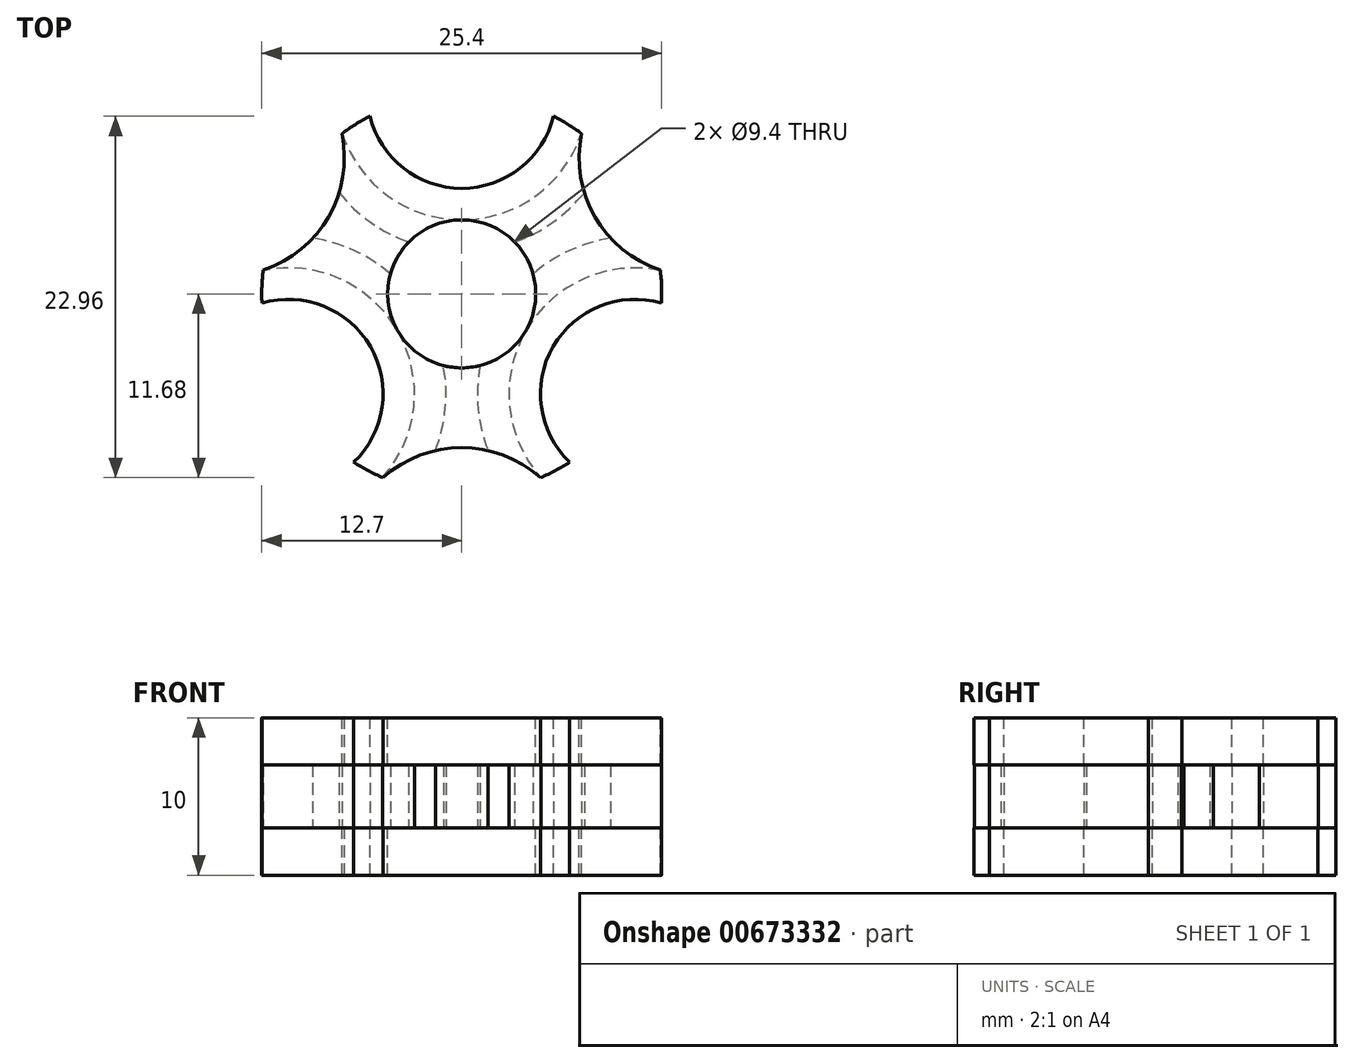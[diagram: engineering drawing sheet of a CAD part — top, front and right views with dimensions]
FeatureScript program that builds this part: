
annotation { "Feature Type Name" : "Feature", "Feature Type Description" : "" }
export const myFeature = defineFeature(function(context is Context, id is Id, definition is map)
    precondition{}
    {
        {
            var Q0;
            Q0=qCreatedBy(makeId("Top.planeOp"),FACE);
            var sketch = newSketch(context, id + "F0", { "sketchPlane" : qUnion([Q0])});
            skLineSegment(sketch, "E0", {"start": v(0, 56.08) * mm, "end": v(0, 0) * mm, "construction": true});
            skLineSegment(sketch, "E1", {"start": v(0, 0) * mm, "end": v(54.15, -31.26) * mm, "construction": true});
            skLineSegment(sketch, "E2", {"start": v(-60, -34.64) * mm, "end": v(0, 0) * mm, "construction": true});
            skLineSegment(sketch, "E3", {"start": v(-56.98, 32.9) * mm, "end": v(-8.46, 4.89) * mm, "construction": true});
            skLineSegment(sketch, "E4", {"start": v(48.6, 28.06) * mm, "end": v(8.46, 4.89) * mm, "construction": true});
            skLineSegment(sketch, "E5", {"start": v(0, -60) * mm, "end": v(0, -9.77) * mm, "construction": true});
            skArc(sketch, "E6", {"start": v(-6.86, -10.7) * mm, "mid": v(-5.8, -3.35) * mm, "end": v(-12.69, -0.6) * mm});
            skArc(sketch, "E7", {"start": v(12.69, -0.6) * mm, "mid": v(5.8, -3.35) * mm, "end": v(6.86, -10.7) * mm});
            skArc(sketch, "E8", {"start": v(-5.83, 11.28) * mm, "mid": v(0, 6.7) * mm, "end": v(5.83, 11.28) * mm});
            skArc(sketch, "E9", {"start": v(-7.6, 10.18) * mm, "mid": v(0, 4.7) * mm, "end": v(7.6, 10.18) * mm});
            skArc(sketch, "E10", {"start": v(12.61, 1.48) * mm, "mid": v(4.07, -2.35) * mm, "end": v(5.02, -11.67) * mm});
            skArc(sketch, "E11", {"start": v(-5.32, -11.99) * mm, "mid": v(-3.96, -2.54) * mm, "end": v(-12.61, 1.48) * mm});
            skArc(sketch, "E12", {"start": v(-5.83, 11.28) * mm, "mid": v(-6.75, 10.76) * mm, "end": v(-7.61, 10.17) * mm});
            skCircle(sketch, "E13", {"center": v(0, 0) * mm, "radius": 4.7 * mm});
            skArc(sketch, "E14", {"start": v(-12.61, 1.51) * mm, "mid": v(-8.46, 4.89) * mm, "end": v(-7.61, 10.17) * mm});
            skArc(sketch, "E15", {"start": v(1.16, -4.56) * mm, "mid": v(1.04, -7.3) * mm, "end": v(1.67, -9.96) * mm});
            skArc(sketch, "E16", {"start": v(-7.79, 6.43) * mm, "mid": v(-5.8, 4.55) * mm, "end": v(-3.36, 3.28) * mm});
            skArc(sketch, "E17.trimOffspring", {"start": v(7.61, 10.17) * mm, "mid": v(8.46, 4.89) * mm, "end": v(12.61, 1.51) * mm});
            skArc(sketch, "E18.trimOffspring", {"start": v(-12.61, 1.51) * mm, "mid": v(-12.7, 0.46) * mm, "end": v(-12.69, -0.6) * mm});
            skArc(sketch, "E19.trimOffspring", {"start": v(-6.86, -10.7) * mm, "mid": v(-5.95, -11.22) * mm, "end": v(-5, -11.68) * mm});
            skArc(sketch, "E20.trimOffspring", {"start": v(-4.53, 1.27) * mm, "mid": v(-6.84, 2.74) * mm, "end": v(-9.46, 3.53) * mm});
            skArc(sketch, "E21.trimOffspring", {"start": v(3.36, 3.28) * mm, "mid": v(5.8, 4.55) * mm, "end": v(7.79, 6.43) * mm});
            skArc(sketch, "E22.trimOffspring", {"start": v(12.69, -0.6) * mm, "mid": v(12.7, 0.46) * mm, "end": v(12.61, 1.51) * mm});
            skArc(sketch, "E23.trimOffspring", {"start": v(5, -11.68) * mm, "mid": v(5.95, -11.22) * mm, "end": v(6.86, -10.7) * mm});
            skArc(sketch, "E24.trimOffspring", {"start": v(7.61, 10.17) * mm, "mid": v(6.75, 10.76) * mm, "end": v(5.83, 11.28) * mm});
            skArc(sketch, "E25.trimOffspring", {"start": v(-1.67, -9.96) * mm, "mid": v(-1.04, -7.3) * mm, "end": v(-1.16, -4.56) * mm});
            skArc(sketch, "E26.trimOffspring", {"start": v(5, -11.68) * mm, "mid": v(-0.22, -9.77) * mm, "end": v(-5.32, -11.99) * mm});
            skArc(sketch, "E27.trimOffspring", {"start": v(9.46, 3.53) * mm, "mid": v(6.84, 2.74) * mm, "end": v(4.53, 1.27) * mm});
            skLineSegment(sketch, "E28.trimOffspring", {"start": v(-4.07, 2.35) * mm, "end": v(0, 0) * mm, "construction": true});
            skLineSegment(sketch, "E29.trimOffspring", {"start": v(4.07, 2.35) * mm, "end": v(0, 0) * mm, "construction": true});
            skLineSegment(sketch, "E30.trimOffspring", {"start": v(0, -4.7) * mm, "end": v(0, 0) * mm, "construction": true});
            skSolve(sketch);
        }
        {
            var Q0;
            {var subQ5=sQuery(id+"F0.wireOp",EDGE,"E6");Q0=makeQuery(id+"F0.imprint","IMPRINT",FACE,{"disambiguationData":[TD([[makeQuery(id+"F0.imprint","IMPRINT",EDGE,{"derivedFrom":subQ5}),-1.0]])]});}
            var Q1;
            {var subQ3=sQuery(id+"F0.wireOp",EDGE,"E20.trimOffspring");Q1=makeQuery(id+"F0.imprint","IMPRINT",FACE,{"disambiguationData":[TD([[makeQuery(id+"F0.imprint","IMPRINT",EDGE,{"derivedFrom":subQ3}),1.0]])]});}
            var Q2;
            {var subQ0=sQuery(id+"F0.wireOp",EDGE,"E16");Q2=makeQuery(id+"F0.imprint","IMPRINT",FACE,{"disambiguationData":[TD([[makeQuery(id+"F0.imprint","IMPRINT",EDGE,{"derivedFrom":subQ0}),-1.0]])]});}
            var Q3;
            {var subQ0=sQuery(id+"F0.wireOp",EDGE,"E16");Q3=makeQuery(id+"F0.imprint","IMPRINT",FACE,{"disambiguationData":[TD([[makeQuery(id+"F0.imprint","IMPRINT",EDGE,{"derivedFrom":subQ0}),1.0]])]});}
            var Q4;
            {var subQ1=sQuery(id+"F0.wireOp",EDGE,"E8");Q4=makeQuery(id+"F0.imprint","IMPRINT",FACE,{"disambiguationData":[TD([[makeQuery(id+"F0.imprint","IMPRINT",EDGE,{"derivedFrom":subQ1}),-1.0]])]});}
            var Q5;
            {var subQ3=sQuery(id+"F0.wireOp",EDGE,"E21.trimOffspring");Q5=makeQuery(id+"F0.imprint","IMPRINT",FACE,{"disambiguationData":[TD([[makeQuery(id+"F0.imprint","IMPRINT",EDGE,{"derivedFrom":subQ3}),1.0]])]});}
            var Q6;
            {var subQ0=sQuery(id+"F0.wireOp",EDGE,"E21.trimOffspring");Q6=makeQuery(id+"F0.imprint","IMPRINT",FACE,{"disambiguationData":[TD([[makeQuery(id+"F0.imprint","IMPRINT",EDGE,{"derivedFrom":subQ0}),-1.0]])]});}
            var Q7;
            {var subQ5=sQuery(id+"F0.wireOp",EDGE,"E27.trimOffspring");Q7=makeQuery(id+"F0.imprint","IMPRINT",FACE,{"disambiguationData":[TD([[makeQuery(id+"F0.imprint","IMPRINT",EDGE,{"derivedFrom":subQ5}),1.0]])]});}
            var Q8;
            {var subQ1=sQuery(id+"F0.wireOp",EDGE,"E7");Q8=makeQuery(id+"F0.imprint","IMPRINT",FACE,{"disambiguationData":[TD([[makeQuery(id+"F0.imprint","IMPRINT",EDGE,{"derivedFrom":subQ1}),-1.0]])]});}
            var Q9;
            {var subQ5=sQuery(id+"F0.wireOp",EDGE,"E15");Q9=makeQuery(id+"F0.imprint","IMPRINT",FACE,{"disambiguationData":[TD([[makeQuery(id+"F0.imprint","IMPRINT",EDGE,{"derivedFrom":subQ5}),1.0]])]});}
            var Q10;
            {var subQ0=sQuery(id+"F0.wireOp",EDGE,"E15");Q10=makeQuery(id+"F0.imprint","IMPRINT",FACE,{"disambiguationData":[TD([[makeQuery(id+"F0.imprint","IMPRINT",EDGE,{"derivedFrom":subQ0}),-1.0]])]});}
            var Q11;
            {var subQ0=sQuery(id+"F0.wireOp",EDGE,"E25.trimOffspring");Q11=makeQuery(id+"F0.imprint","IMPRINT",FACE,{"disambiguationData":[TD([[makeQuery(id+"F0.imprint","IMPRINT",EDGE,{"derivedFrom":subQ0}),1.0]])]});}
            extrude(context, id + "F1", {"entities" : qUnion([Q0, Q1, Q2, Q3, Q4, Q5, Q6, Q7, Q8, Q9, Q10, Q11]), "oppositeDirection" : true, "depth" : 3 * mm, "offsetDistance" : 25 * mm});
        }
        {
            var Q0;
            {var subQ1=sQuery(id+"F0.wireOp",EDGE,"E7");Q0=makeQuery(id+"F0.imprint","IMPRINT",FACE,{"disambiguationData":[TD([[makeQuery(id+"F0.imprint","IMPRINT",EDGE,{"derivedFrom":subQ1}),-1.0]])]});}
            var Q1;
            {var subQ0=sQuery(id+"F0.wireOp",EDGE,"E15");Q1=makeQuery(id+"F0.imprint","IMPRINT",FACE,{"disambiguationData":[TD([[makeQuery(id+"F0.imprint","IMPRINT",EDGE,{"derivedFrom":subQ0}),-1.0]])]});}
            var Q2;
            {var subQ5=sQuery(id+"F0.wireOp",EDGE,"E6");Q2=makeQuery(id+"F0.imprint","IMPRINT",FACE,{"disambiguationData":[TD([[makeQuery(id+"F0.imprint","IMPRINT",EDGE,{"derivedFrom":subQ5}),-1.0]])]});}
            var Q3;
            {var subQ0=sQuery(id+"F0.wireOp",EDGE,"E16");Q3=makeQuery(id+"F0.imprint","IMPRINT",FACE,{"disambiguationData":[TD([[makeQuery(id+"F0.imprint","IMPRINT",EDGE,{"derivedFrom":subQ0}),-1.0]])]});}
            var Q4;
            {var subQ1=sQuery(id+"F0.wireOp",EDGE,"E8");Q4=makeQuery(id+"F0.imprint","IMPRINT",FACE,{"disambiguationData":[TD([[makeQuery(id+"F0.imprint","IMPRINT",EDGE,{"derivedFrom":subQ1}),-1.0]])]});}
            var Q5;
            {var subQ0=sQuery(id+"F0.wireOp",EDGE,"E21.trimOffspring");Q5=makeQuery(id+"F0.imprint","IMPRINT",FACE,{"disambiguationData":[TD([[makeQuery(id+"F0.imprint","IMPRINT",EDGE,{"derivedFrom":subQ0}),-1.0]])]});}
            extrude(context, id + "F2", {"entities" : qUnion([Q0, Q1, Q2, Q3, Q4, Q5]), "depth" : 4 * mm, "offsetDistance" : 25 * mm});
        }
        {
            var Q0;
            Q0=makeQuery(id+"F1.opExtrude","SWEPT_BODY",BODY,{"disambiguationData":[OSD([sQuery(id+"F0.wireOp",EDGE,"E6"),sQuery(id+"F0.wireOp",EDGE,"E7"),sQuery(id+"F0.wireOp",EDGE,"E8"),sQuery(id+"F0.wireOp",EDGE,"E12"),sQuery(id+"F0.wireOp",EDGE,"E13"),sQuery(id+"F0.wireOp",EDGE,"E14"),sQuery(id+"F0.wireOp",EDGE,"E17.trimOffspring"),sQuery(id+"F0.wireOp",EDGE,"E18.trimOffspring"),sQuery(id+"F0.wireOp",EDGE,"E19.trimOffspring"),sQuery(id+"F0.wireOp",EDGE,"E22.trimOffspring"),sQuery(id+"F0.wireOp",EDGE,"E23.trimOffspring"),sQuery(id+"F0.wireOp",EDGE,"E24.trimOffspring"),sQuery(id+"F0.wireOp",EDGE,"E26.trimOffspring")])]});
            transform(context, id + "F3", {"entities" : qUnion([Q0]), "transformType" : TransformType.TRANSLATION_3D, "dx" : 0 * mm, "dy" : 0 * mm, "dz" : 7 * mm, "makeCopy" : true});
        }
    });
